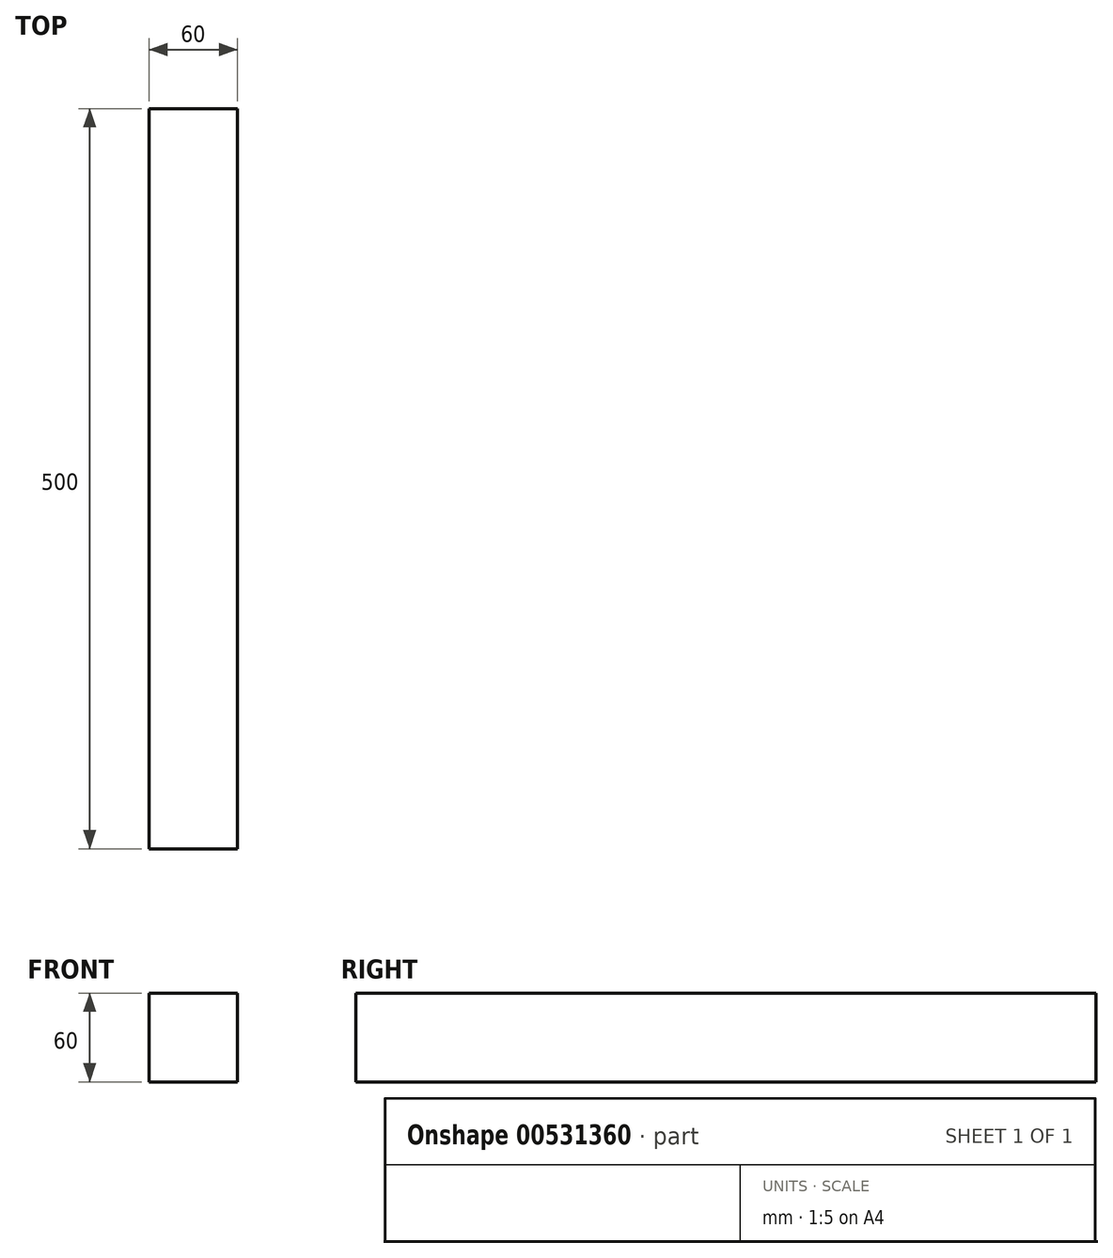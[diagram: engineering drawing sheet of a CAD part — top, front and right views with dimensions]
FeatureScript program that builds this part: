
annotation { "Feature Type Name" : "Feature", "Feature Type Description" : "" }
export const myFeature = defineFeature(function(context is Context, id is Id, definition is map)
    precondition{}
    {
        {
            var Q0;
            Q0=qCreatedBy(makeId("Top.planeOp"),FACE);
            var sketch = newSketch(context, id + "F0", { "sketchPlane" : qUnion([Q0])});
            skLineSegment(sketch, "E0.bottom", {"start": v(0, 0) * mm, "end": v(60, 0) * mm});
            skLineSegment(sketch, "E0.top", {"start": v(0, 500) * mm, "end": v(60, 500) * mm});
            skLineSegment(sketch, "E0.left", {"start": v(0, 0) * mm, "end": v(0, 500) * mm});
            skLineSegment(sketch, "E0.right", {"start": v(60, 0) * mm, "end": v(60, 500) * mm});
            skSolve(sketch);
        }
        {
            var Q0;
            Q0=makeQuery(id+"F0.imprint","IMPRINT",FACE,{"disambiguationData":[TD([[makeQuery(id+"F0.imprint","IMPRINT",EDGE,{"derivedFrom":sQuery(id+"F0.wireOp",EDGE,"E0.bottom")}),1.0]])]});
            extrude(context, id + "F1", {"entities" : qUnion([Q0]), "depth" : 60 * mm, "offsetDistance" : 25 * mm});
        }
    });
